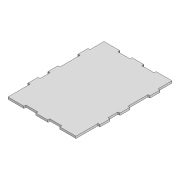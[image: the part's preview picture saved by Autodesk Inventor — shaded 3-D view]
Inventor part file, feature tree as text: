
AUTODESK INVENTOR PART (.ipt)
format: ipt  version: 2022 (Build 260153000, 153)  size: 147,456 bytes
history: native  units: mm
features: extrude x1, sketch x1
ambient origin geometry x8: Origin, YZ Plane, XZ Plane, XY Plane, X Axis, Y Axis, Z Axis, Center Point
bodies: Solid1 (feature_tree)
feature tree (2):
  extrude  "Extrusion1"  Depth=240.0mm
  sketch  "Sketch1"  dims[d0=170.0mm d1=240.0mm d2=5.0mm d3=25.0mm d4=5.0mm d5=25.0mm d6=5.0mm d7=25.0mm d8=35.0mm d9=50.0mm d10=25.0mm d11=30.0mm d12=30.0mm d13=5.0mm d14=5.0mm d15=30.0mm d16=15.0mm d17=5.0mm d18=5.0mm d19=0.0mm d20=10.0mm d21=10.0mm d22=0.5mm d23=0.872665mm d24=0.5mm d25=0.872665mm]
